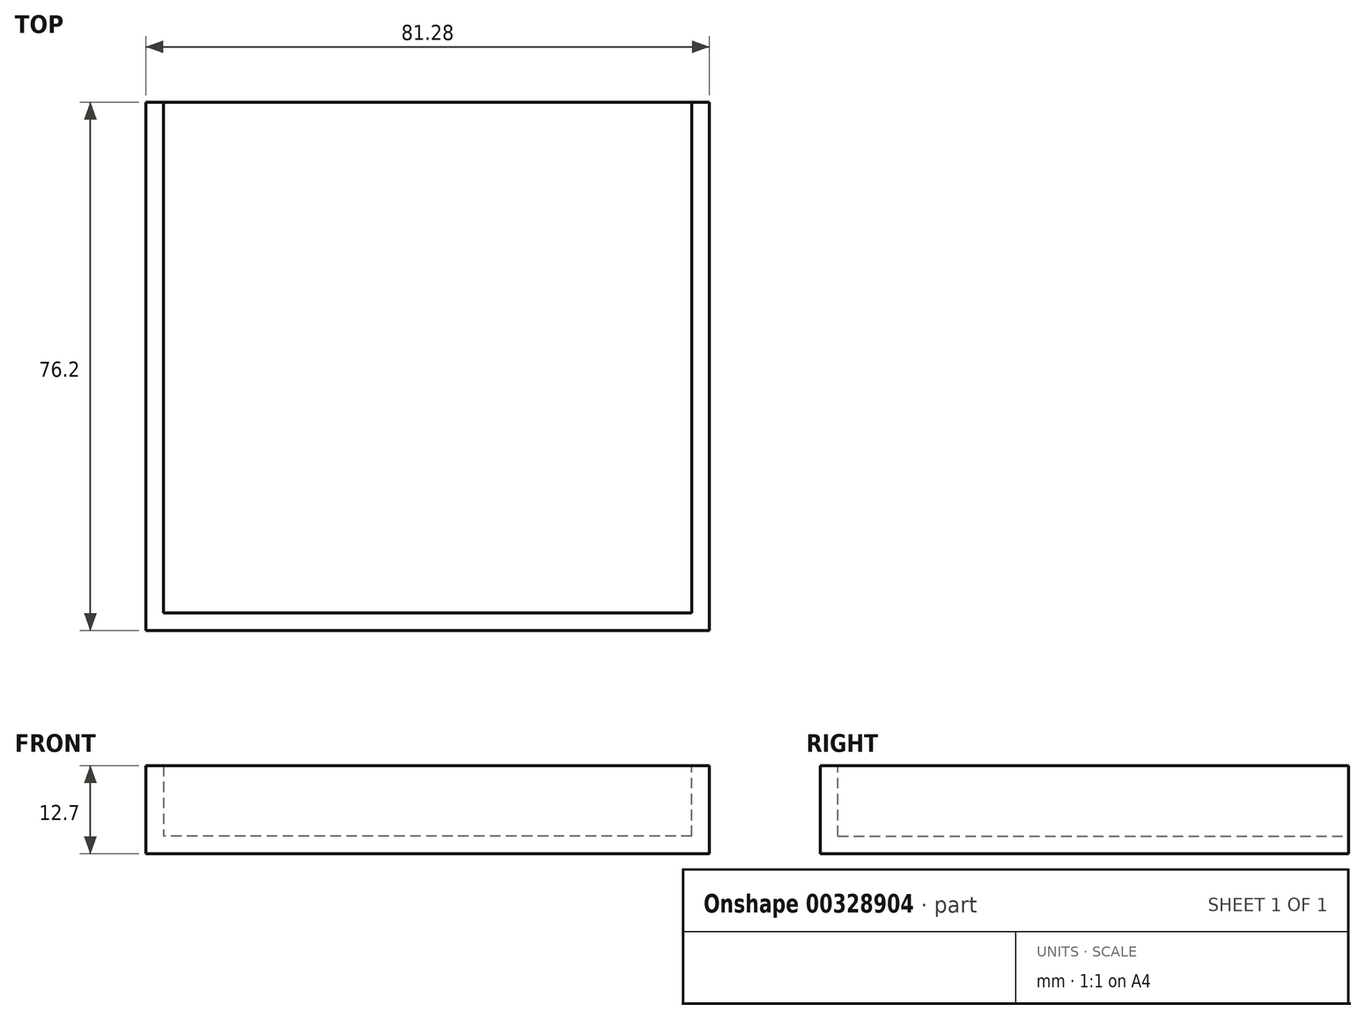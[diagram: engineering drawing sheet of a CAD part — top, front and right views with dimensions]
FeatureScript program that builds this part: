
annotation { "Feature Type Name" : "Feature", "Feature Type Description" : "" }
export const myFeature = defineFeature(function(context is Context, id is Id, definition is map)
    precondition{}
    {
        {
            var Q0;
            Q0=qCreatedBy(makeId("Front.planeOp"),FACE);
            var sketch = newSketch(context, id + "F0", { "sketchPlane" : qUnion([Q0])});
            skLineSegment(sketch, "E0", {"start": v(38.28, 0) * mm, "end": v(-37.92, 0) * mm});
            skLineSegment(sketch, "E1", {"start": v(-37.92, 0) * mm, "end": v(-37.92, -2.54) * mm});
            skLineSegment(sketch, "E2", {"start": v(-37.92, -2.54) * mm, "end": v(38.28, -2.54) * mm});
            skLineSegment(sketch, "E3", {"start": v(38.28, -2.54) * mm, "end": v(38.28, 0) * mm});
            skLineSegment(sketch, "E4", {"start": v(-37.92, -2.54) * mm, "end": v(-40.46, -2.54) * mm});
            skLineSegment(sketch, "E5", {"start": v(-40.46, -2.54) * mm, "end": v(-40.46, 10.16) * mm});
            skLineSegment(sketch, "E6", {"start": v(-40.46, 10.16) * mm, "end": v(-37.92, 10.16) * mm});
            skLineSegment(sketch, "E7", {"start": v(-37.92, 10.16) * mm, "end": v(-37.92, 0) * mm});
            skLineSegment(sketch, "E8", {"start": v(38.28, 0) * mm, "end": v(38.28, 10.16) * mm});
            skLineSegment(sketch, "E9", {"start": v(38.28, 10.16) * mm, "end": v(40.82, 10.16) * mm});
            skLineSegment(sketch, "E10", {"start": v(40.82, 10.16) * mm, "end": v(40.82, -2.54) * mm});
            skLineSegment(sketch, "E11", {"start": v(40.82, -2.54) * mm, "end": v(38.28, -2.54) * mm});
            skSolve(sketch);
        }
        {
            var Q0;
            Q0=makeQuery(id+"F0.imprint","IMPRINT",FACE,{"disambiguationData":[TD([[makeQuery(id+"F0.imprint","IMPRINT",EDGE,{"derivedFrom":sQuery(id+"F0.wireOp",EDGE,"E0")}),1.0]])]});
            extrude(context, id + "F1", {"entities" : qUnion([Q0]), "depth" : 76.2 * mm});
        }
        {
            var Q0;
            Q0=makeQuery(id+"F0.imprint","IMPRINT",FACE,{"disambiguationData":[TD([[makeQuery(id+"F0.imprint","IMPRINT",EDGE,{"derivedFrom":sQuery(id+"F0.wireOp",EDGE,"E1")}),-1.0]])]});
            extrude(context, id + "F2", {"entities" : qUnion([Q0]), "operationType" : NewBodyOperationType.ADD, "depth" : 76.2 * mm});
        }
        {
            var Q0;
            Q0=makeQuery(id+"F0.imprint","IMPRINT",FACE,{"disambiguationData":[TD([[makeQuery(id+"F0.imprint","IMPRINT",EDGE,{"derivedFrom":sQuery(id+"F0.wireOp",EDGE,"E3")}),-1.0]])]});
            extrude(context, id + "F3", {"entities" : qUnion([Q0]), "operationType" : NewBodyOperationType.ADD, "depth" : 76.2 * mm});
        }
        {
            var Q0;
            Q0=makeQuery(id+"F2.opExtrude","SWEPT_FACE",FACE,{"disambiguationData":[OSD([sQuery(id+"F0.wireOp",EDGE,"E1"),sQuery(id+"F0.wireOp",EDGE,"E7")])]});
            var sketch = newSketch(context, id + "F4", { "sketchPlane" : qUnion([Q0])});
            skLineSegment(sketch, "E12", {"start": v(-76.2, 10.16) * mm, "end": v(-76.2, 0) * mm});
            skLineSegment(sketch, "E13", {"start": v(-76.2, 0) * mm, "end": v(-73.66, 0) * mm});
            skLineSegment(sketch, "E14", {"start": v(-73.66, 0) * mm, "end": v(-73.66, 10.16) * mm});
            skLineSegment(sketch, "E15", {"start": v(-73.66, 10.16) * mm, "end": v(-76.2, 10.16) * mm});
            skSolve(sketch);
        }
        {
            var Q0;
            Q0=makeQuery(id+"F4.imprint","IMPRINT",FACE,{"disambiguationData":[TD([[makeQuery(id+"F4.imprint","IMPRINT",EDGE,{"derivedFrom":sQuery(id+"F4.wireOp",EDGE,"E12")}),1.0]])]});
            extrude(context, id + "F5", {"entities" : qUnion([Q0]), "operationType" : NewBodyOperationType.ADD, "depth" : 76.2 * mm});
        }
    });
